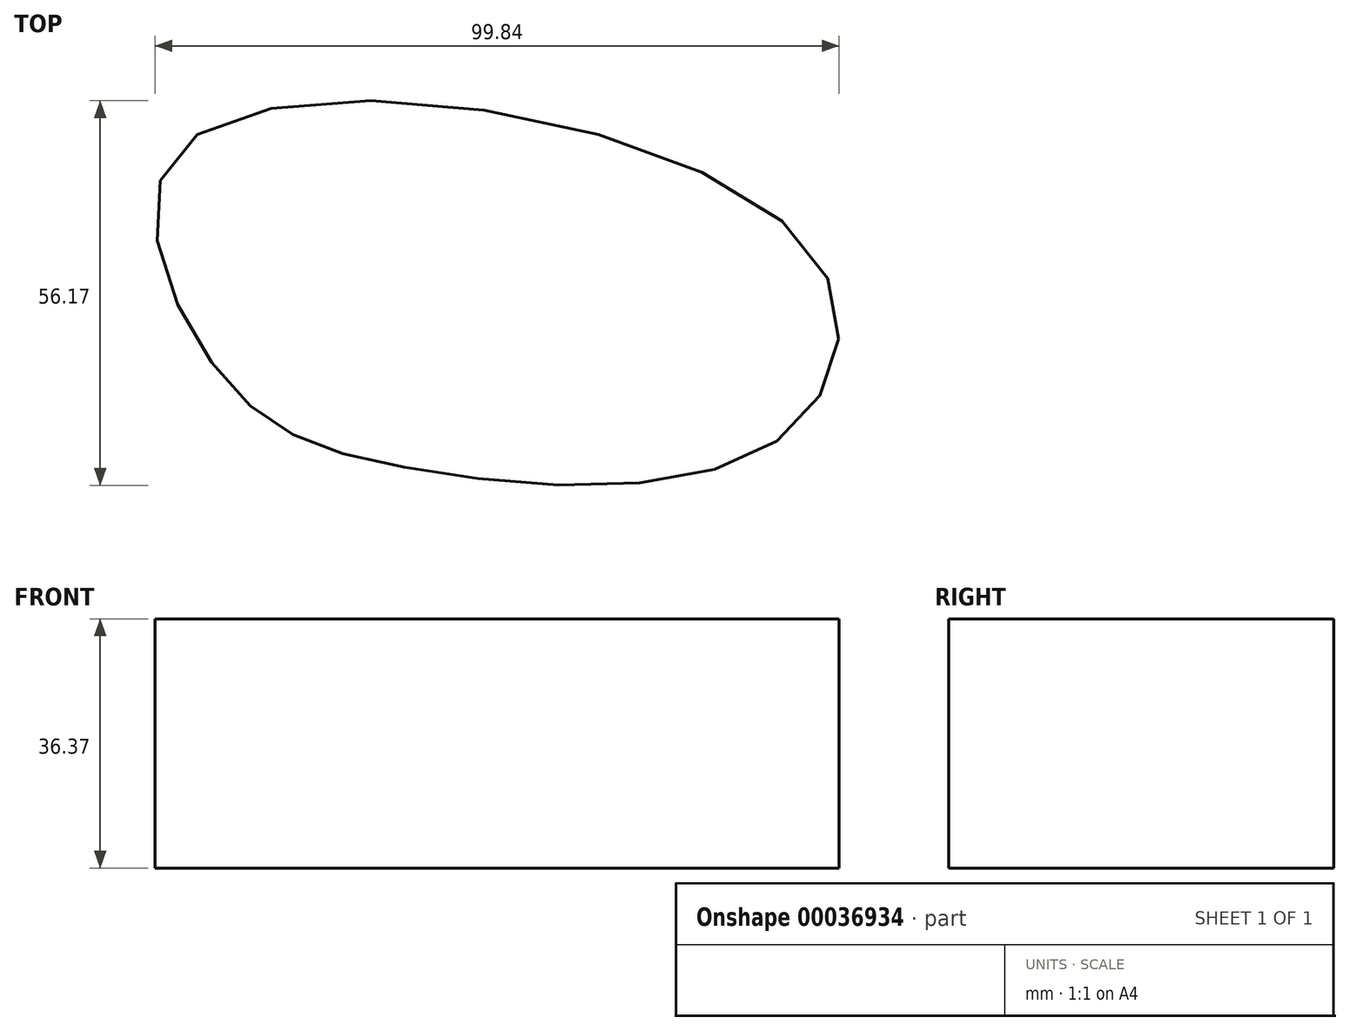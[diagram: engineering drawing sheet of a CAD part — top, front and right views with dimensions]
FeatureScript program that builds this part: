
annotation { "Feature Type Name" : "Feature", "Feature Type Description" : "" }
export const myFeature = defineFeature(function(context is Context, id is Id, definition is map)
    precondition{}
    {
        {
            var Q0;
            Q0=qCreatedBy(makeId("Top.planeOp"),FACE);
            var sketch = newSketch(context, id + "F0", { "sketchPlane" : qUnion([Q0])});
            skFitSpline(sketch, "E0", {"points": [v(39.65, -9.84) * mm, v(-15.4, -13.55) * mm, v(-41.65, 0) * mm, v(-46.78, 33.52) * mm, v(42.5, 20.4) * mm, v(39.65, -9.84) * mm]});
            skSolve(sketch);
        }
        {
            var Q0;
            Q0=makeQuery(id+"F0.imprint","IMPRINT",FACE,{"disambiguationData":[TD([[makeQuery(id+"F0.imprint","IMPRINT",EDGE,{"derivedFrom":sQuery(id+"F0.wireOp",EDGE,"E0")}),-1.0]])]});
            extrude(context, id + "F1", {"entities" : qUnion([Q0]), "depth" : 36.37 * mm});
        }
    });
